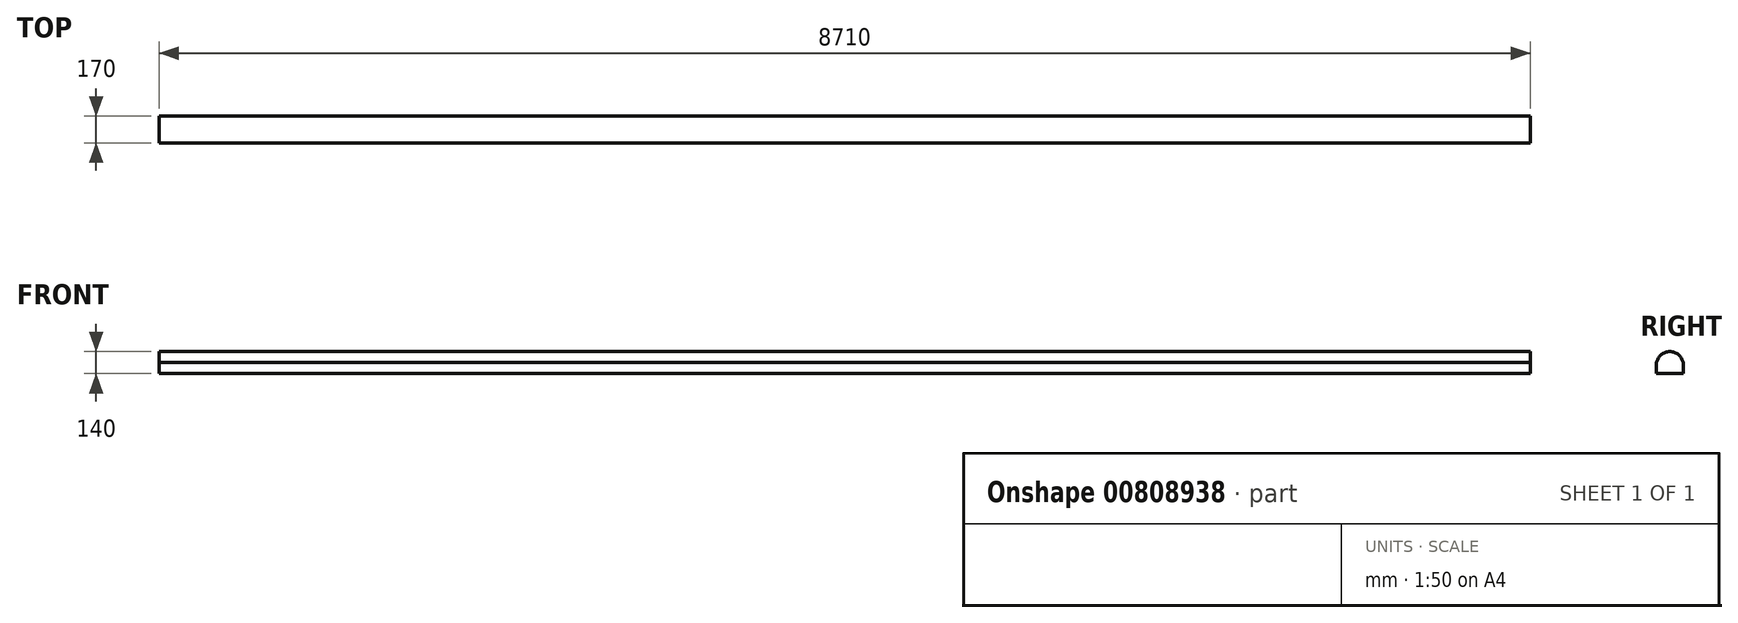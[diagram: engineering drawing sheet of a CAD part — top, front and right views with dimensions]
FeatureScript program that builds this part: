
annotation { "Feature Type Name" : "Feature", "Feature Type Description" : "" }
export const myFeature = defineFeature(function(context is Context, id is Id, definition is map)
    precondition{}
    {
        {
            var Q0;
            Q0=qCreatedBy(makeId("Right.planeOp"),FACE);
            var sketch = newSketch(context, id + "F0", { "sketchPlane" : qUnion([Q0])});
            skLineSegment(sketch, "E0.bottom", {"start": v(85, -70) * mm, "end": v(-85, -70) * mm, "construction": true});
            skLineSegment(sketch, "E0.top", {"start": v(85, 70) * mm, "end": v(-85, 70) * mm, "construction": true});
            skLineSegment(sketch, "E0.left", {"start": v(85, -70) * mm, "end": v(85, 70) * mm, "construction": true});
            skLineSegment(sketch, "E0.right", {"start": v(-85, -70) * mm, "end": v(-85, 70) * mm, "construction": true});
            skPoint(sketch, "E0.middle", {"position": v(0, 0) * mm});
            skPoint(sketch, "E1.first.point", {"position": v(0, 70) * mm});
            skPoint(sketch, "E1.second.point", {"position": v(-85, 0) * mm});
            skPoint(sketch, "E1.third.point", {"position": v(85, 0) * mm});
            skLineSegment(sketch, "E2.bottom", {"start": v(-85, -70) * mm, "end": v(85, -70) * mm});
            skLineSegment(sketch, "E2.top", {"start": v(-85, 0) * mm, "end": v(85, 0) * mm});
            skLineSegment(sketch, "E2.left", {"start": v(-85, -70) * mm, "end": v(-85, 0) * mm});
            skLineSegment(sketch, "E2.right", {"start": v(85, -70) * mm, "end": v(85, 0) * mm});
            skArc(sketch, "E3.trimOffspring", {"start": v(85, 0) * mm, "mid": v(0, 70) * mm, "end": v(-85, 0) * mm});
            skSolve(sketch);
        }
        {
            var Q0;
            Q0 = qSketchRegion(id + "F0", true);
            extrude(context, id + "F1", {"entities" : qUnion([Q0]), "depth" : 8710 * mm, "offsetDistance" : 25 * mm});
        }
    });
